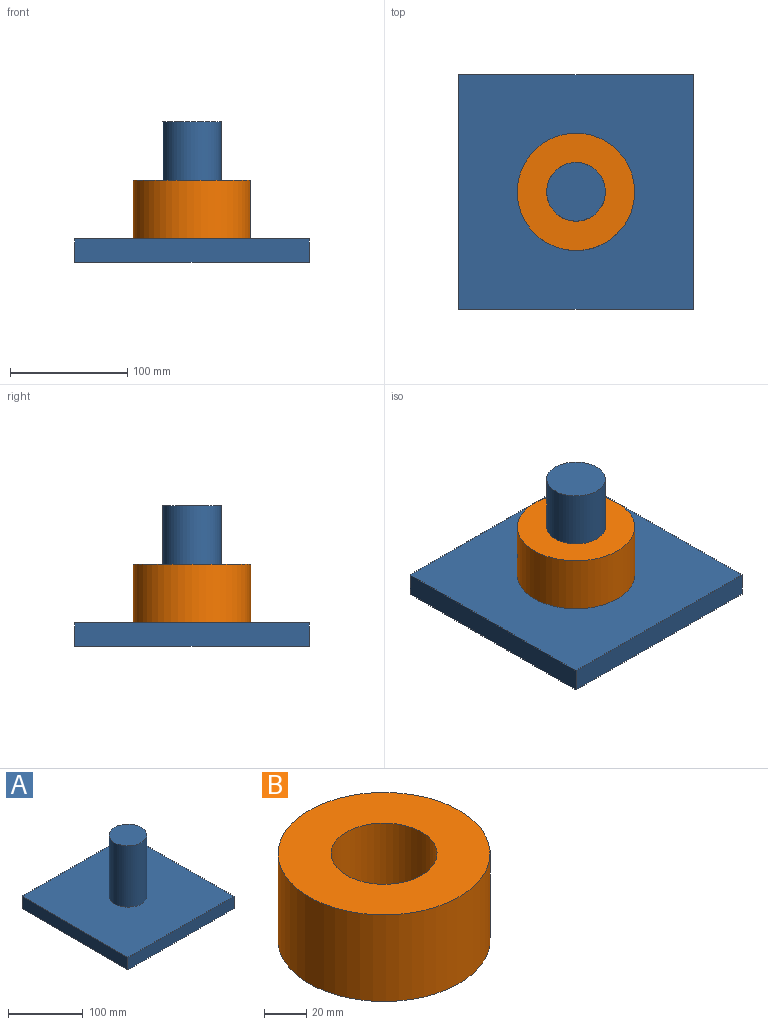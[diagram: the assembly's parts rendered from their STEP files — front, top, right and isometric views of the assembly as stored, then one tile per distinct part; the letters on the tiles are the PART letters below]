
ASSEMBLY  parts=2 mates=1
PART A: 8 faces, bbox 200x200x120 mm
  f0: plane 200x20mm, normal (-1,0,0), area 4000mm2, adj f1,f3,f4,f5
  f1: plane 200x20mm, normal (0,-1,0), area 4000mm2, adj f0,f2,f4,f5
  f2: plane 200x20mm, normal (1,0,0), area 4000mm2, adj f1,f3,f4,f5
  f3: plane 200x20mm, normal (0,1,0), area 4000mm2, adj f0,f2,f4,f5
  f4: plane 200x200mm, normal (0,0,1), area 38036.5mm2, adj f0,f1,f2,f3,f6
  f5: plane 200x200mm, normal (0,0,-1), area 40000mm2, adj f0,f1,f2,f3
  f6: cylinder r=25mm len=100mm, axis (0,0,-1), area 15708mm2, adj f4,f7
  f7: plane 50x50mm, normal (0,0,1), area 1963.5mm2, adj f6
PART B: 4 faces, bbox 100x100x50 mm
  f0: cylinder r=25mm len=50mm, axis (0,0,-1), area 7854mm2, adj f2,f3
  f1: cylinder r=50mm len=100mm, axis (0,0,-1), area 15708mm2, adj f2,f3
  f2: plane 100x100mm, normal (0,0,1), area 5890.5mm2, adj f0,f1
  f3: plane 100x100mm, normal (0,0,-1), area 5890.5mm2, adj f0,f1
PLACE A t=(-94.64,183.35,75.39)mm fixed
PLACE B rot(axis=(0,0,1),180deg) t=(5.36,83.35,95.39)mm
MATE revolute A.f6 <-> B.f0  axis (0,0,1) through (5.36,83.35,95.39)mm
